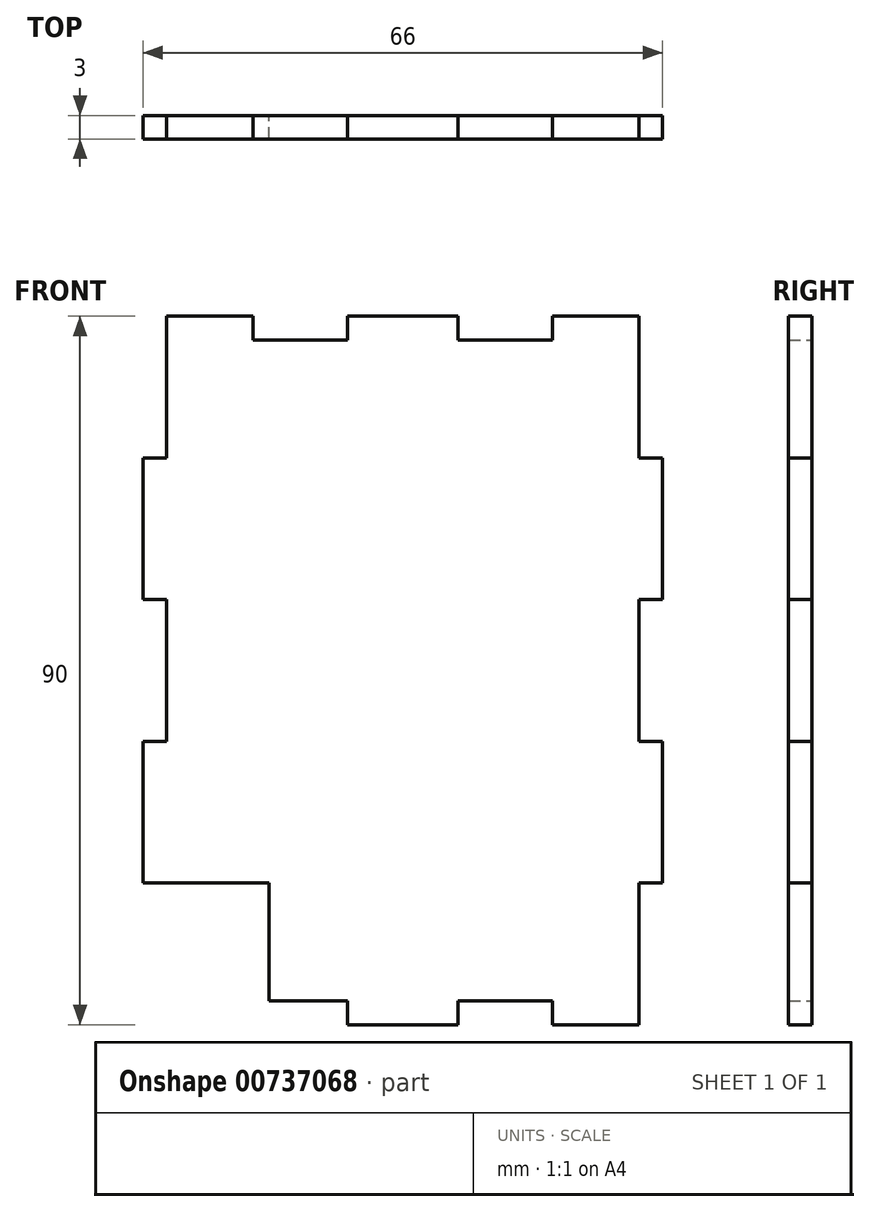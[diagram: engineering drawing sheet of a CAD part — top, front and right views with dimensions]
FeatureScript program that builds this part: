
annotation { "Feature Type Name" : "Feature", "Feature Type Description" : "" }
export const myFeature = defineFeature(function(context is Context, id is Id, definition is map)
    precondition{}
    {
        {
            var Q0;
            Q0=qCreatedBy(makeId("Front.planeOp"),FACE);
            var sketch = newSketch(context, id + "F0", { "sketchPlane" : qUnion([Q0])});
            skLineSegment(sketch, "E0.bottom", {"start": v(33, -45) * mm, "end": v(-33, -45) * mm, "construction": true});
            skLineSegment(sketch, "E0.top", {"start": v(33, 45) * mm, "end": v(-33, 45) * mm, "construction": true});
            skPoint(sketch, "E0.middle", {"position": v(0, 0) * mm});
            skLineSegment(sketch, "E1", {"start": v(-33, 45) * mm, "end": v(-19, 45) * mm});
            skLineSegment(sketch, "E2", {"start": v(-19, 45) * mm, "end": v(-19, 42) * mm});
            skLineSegment(sketch, "E3", {"start": v(-19, 42) * mm, "end": v(-7, 42) * mm});
            skLineSegment(sketch, "E4", {"start": v(-7, 42) * mm, "end": v(-7, 45) * mm});
            skLineSegment(sketch, "E5", {"start": v(-7, 45) * mm, "end": v(7, 45) * mm});
            skLineSegment(sketch, "E6", {"start": v(7, 45) * mm, "end": v(7, 42) * mm});
            skLineSegment(sketch, "E7", {"start": v(7, 42) * mm, "end": v(19, 42) * mm});
            skLineSegment(sketch, "E8", {"start": v(19, 42) * mm, "end": v(19, 45) * mm});
            skLineSegment(sketch, "E9", {"start": v(19, 45) * mm, "end": v(33, 45) * mm});
            skLineSegment(sketch, "E10", {"start": v(-33, -45) * mm, "end": v(-19, -45) * mm, "construction": true});
            skLineSegment(sketch, "E11", {"start": v(-19, -45) * mm, "end": v(-19, -42) * mm, "construction": true});
            skLineSegment(sketch, "E12", {"start": v(-19, -42) * mm, "end": v(-7, -42) * mm});
            skLineSegment(sketch, "E13", {"start": v(-7, -42) * mm, "end": v(-7, -45) * mm});
            skLineSegment(sketch, "E14", {"start": v(-7, -45) * mm, "end": v(7, -45) * mm});
            skLineSegment(sketch, "E15", {"start": v(7, -45) * mm, "end": v(7, -42) * mm});
            skLineSegment(sketch, "E16", {"start": v(7, -42) * mm, "end": v(19, -42) * mm});
            skLineSegment(sketch, "E17", {"start": v(19, -42) * mm, "end": v(19, -45) * mm});
            skLineSegment(sketch, "E18", {"start": v(19, -45) * mm, "end": v(33, -45) * mm});
            skLineSegment(sketch, "E19", {"start": v(-33, 45) * mm, "end": v(-33, -45) * mm, "construction": true});
            skLineSegment(sketch, "E20", {"start": v(-30, 45) * mm, "end": v(-30, 27) * mm});
            skLineSegment(sketch, "E21", {"start": v(-30, 27) * mm, "end": v(-33, 27) * mm});
            skLineSegment(sketch, "E22", {"start": v(-33, 27) * mm, "end": v(-33, 9) * mm});
            skLineSegment(sketch, "E23", {"start": v(-33, 9) * mm, "end": v(-30, 9) * mm});
            skLineSegment(sketch, "E24", {"start": v(-30, 9) * mm, "end": v(-30, -9) * mm});
            skLineSegment(sketch, "E25", {"start": v(-30, -9) * mm, "end": v(-33, -9) * mm});
            skLineSegment(sketch, "E26", {"start": v(-33, -9) * mm, "end": v(-33, -27) * mm});
            skLineSegment(sketch, "E27", {"start": v(-33, -27) * mm, "end": v(-30, -27) * mm});
            skLineSegment(sketch, "E28", {"start": v(-30, -27) * mm, "end": v(-30, -45) * mm, "construction": true});
            skLineSegment(sketch, "E29", {"start": v(33, 45) * mm, "end": v(33, -45) * mm, "construction": true});
            skLineSegment(sketch, "E30", {"start": v(30, 45) * mm, "end": v(30, 27) * mm});
            skLineSegment(sketch, "E31", {"start": v(30, 27) * mm, "end": v(33, 27) * mm});
            skLineSegment(sketch, "E32", {"start": v(33, 27) * mm, "end": v(33, 9) * mm});
            skLineSegment(sketch, "E33", {"start": v(33, 9) * mm, "end": v(30, 9) * mm});
            skLineSegment(sketch, "E34", {"start": v(30, 9) * mm, "end": v(30, -9) * mm});
            skLineSegment(sketch, "E35", {"start": v(30, -9) * mm, "end": v(33, -9) * mm});
            skLineSegment(sketch, "E36", {"start": v(33, -9) * mm, "end": v(33, -27) * mm});
            skLineSegment(sketch, "E37", {"start": v(33, -27) * mm, "end": v(30, -27) * mm});
            skLineSegment(sketch, "E38", {"start": v(30, -27) * mm, "end": v(30, -45) * mm});
            skLineSegment(sketch, "E39", {"start": v(-17, -42) * mm, "end": v(-17, -27) * mm});
            skLineSegment(sketch, "E40", {"start": v(-30, -27) * mm, "end": v(-17, -27) * mm});
            skSolve(sketch);
        }
        {
            var Q0;
            Q0=makeQuery(id+"F0.imprint","IMPRINT",FACE,{"disambiguationData":[TD([[makeQuery(id+"F0.imprint","IMPRINT",EDGE,{"derivedFrom":sQuery(id+"F0.wireOp",EDGE,"E1")}),-1.0]])]});
            extrude(context, id + "F1", {"entities" : qUnion([Q0]), "depth" : 3 * mm, "offsetDistance" : 25 * mm});
        }
    });
